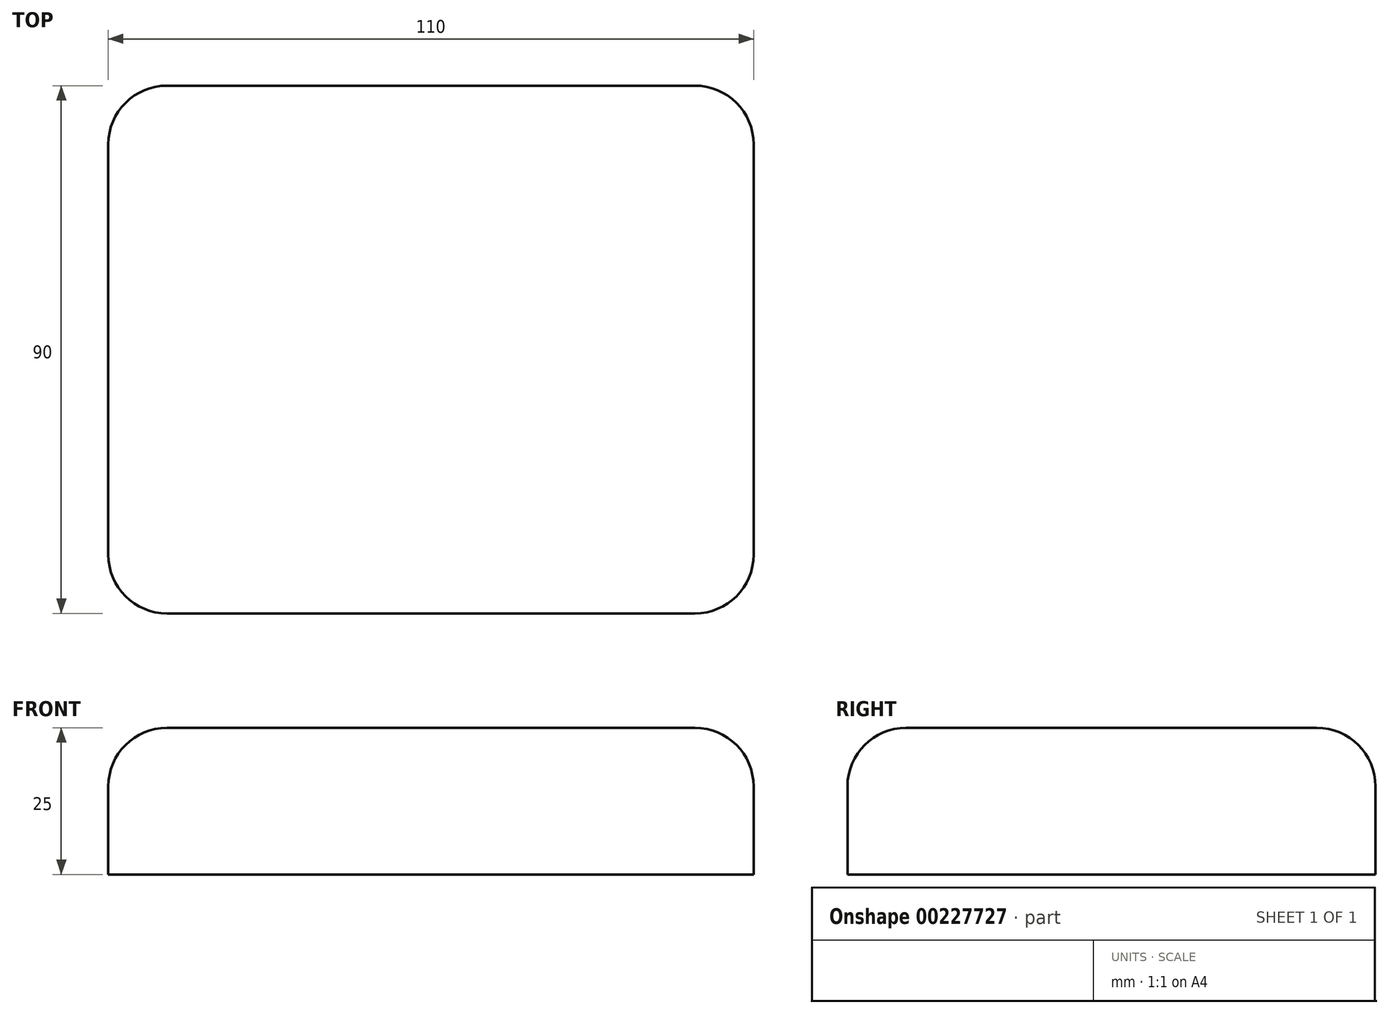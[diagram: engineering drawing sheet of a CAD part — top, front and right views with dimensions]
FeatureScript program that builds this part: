
annotation { "Feature Type Name" : "Feature", "Feature Type Description" : "" }
export const myFeature = defineFeature(function(context is Context, id is Id, definition is map)
    precondition{}
    {
        {
            var Q0;
            Q0=qCreatedBy(makeId("Top.planeOp"),FACE);
            var sketch = newSketch(context, id + "F0", { "sketchPlane" : qUnion([Q0])});
            skLineSegment(sketch, "E0.bottom", {"start": v(55, -45) * mm, "end": v(-55, -45) * mm});
            skLineSegment(sketch, "E0.top", {"start": v(55, 45) * mm, "end": v(-55, 45) * mm});
            skLineSegment(sketch, "E0.left", {"start": v(55, -45) * mm, "end": v(55, 45) * mm});
            skLineSegment(sketch, "E0.right", {"start": v(-55, -45) * mm, "end": v(-55, 45) * mm});
            skPoint(sketch, "E0.middle", {"position": v(0, 0) * mm});
            skSolve(sketch);
        }
        {
            var Q0;
            Q0=makeQuery(id+"F0.imprint","IMPRINT",FACE,{"disambiguationData":[TD([[makeQuery(id+"F0.imprint","IMPRINT",EDGE,{"derivedFrom":sQuery(id+"F0.wireOp",EDGE,"E0.bottom")}),-1.0]])]});
            extrude(context, id + "F1", {"entities" : qUnion([Q0]), "depth" : 25 * mm});
        }
        {
            var Q0;
            Q0=makeQuery(id+"F1.opExtrude","CAP_FACE",FACE,{"disambiguationData":[OSD([sQuery(id+"F0.wireOp",EDGE,"E0.bottom"),sQuery(id+"F0.wireOp",EDGE,"E0.top"),sQuery(id+"F0.wireOp",EDGE,"E0.left"),sQuery(id+"F0.wireOp",EDGE,"E0.right")])],"isStart":false});
            var Q1;
            Q1=makeQuery(id+"F1.opExtrude","SWEPT_EDGE",EDGE,{"disambiguationData":[OSD([sQuery(id+"F0.wireOp",EDGE,"E0.top"),sQuery(id+"F0.wireOp",EDGE,"E0.right")])]});
            var Q2;
            Q2=makeQuery(id+"F1.opExtrude","SWEPT_EDGE",EDGE,{"disambiguationData":[OSD([sQuery(id+"F0.wireOp",EDGE,"E0.bottom"),sQuery(id+"F0.wireOp",EDGE,"E0.right")])]});
            var Q3;
            Q3=makeQuery(id+"F1.opExtrude","SWEPT_EDGE",EDGE,{"disambiguationData":[OSD([sQuery(id+"F0.wireOp",EDGE,"E0.bottom"),sQuery(id+"F0.wireOp",EDGE,"E0.left")])]});
            var Q4;
            Q4=makeQuery(id+"F1.opExtrude","SWEPT_EDGE",EDGE,{"disambiguationData":[OSD([sQuery(id+"F0.wireOp",EDGE,"E0.top"),sQuery(id+"F0.wireOp",EDGE,"E0.left")])]});
            fillet(context, id + "F2", {"entities" : qUnion([Q0, Q1, Q2, Q3, Q4]), "radius" : 10 * mm, "tangentPropagation" : true, "allowEdgeOverflow" : false});
        }
    });
